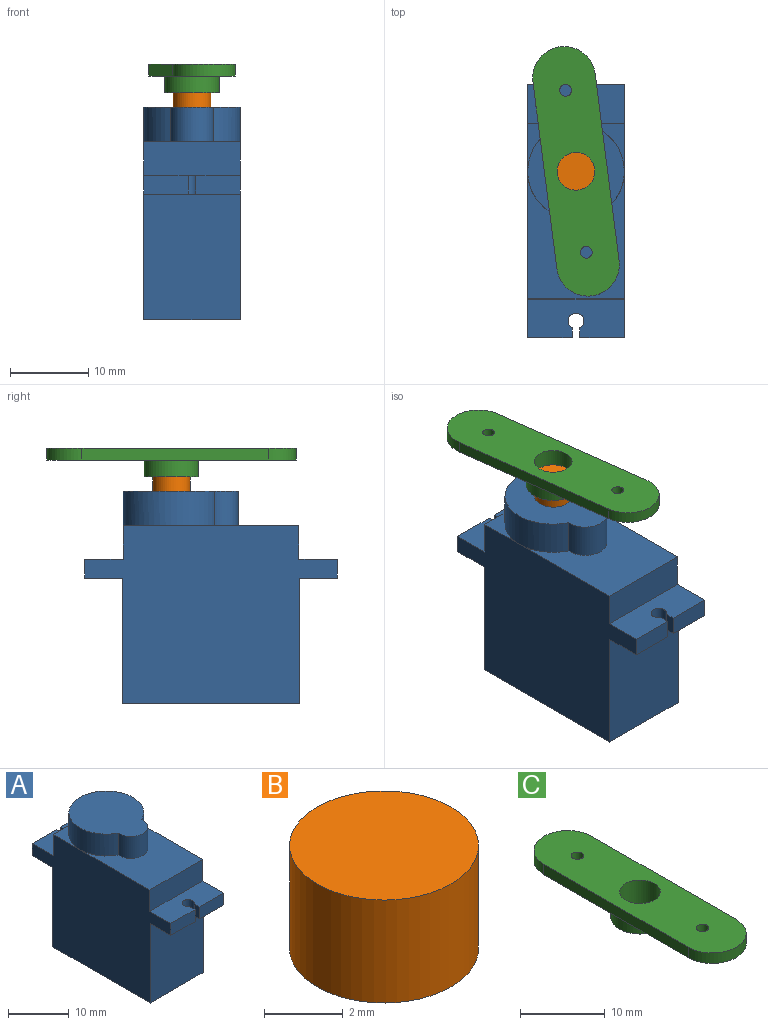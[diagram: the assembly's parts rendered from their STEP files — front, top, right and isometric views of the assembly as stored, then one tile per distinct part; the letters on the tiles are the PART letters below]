
ASSEMBLY  parts=3 mates=2
PART A: 27 faces, bbox 12.3x32.2x27.1 mm
  f0: plane 12.3x4.8mm, normal (0,0,-1), area 54.8mm2, adj f5,f11,f12,f13,f14,f15,f16,f24
  f1: plane 16.25x12.3mm, normal (0,0,1), area 129.6mm2, adj f5,f11,f19,f21,f22
  f2: plane 6.15x6.15mm, normal (0,0,1), area 8.1mm2, adj f5,f20,f21
  f3: plane 6.15x6.15mm, normal (0,0,1), area 8.1mm2, adj f11,f20,f21
  f4: plane 12.3x4.9mm, normal (0,0,1), area 56mm2, adj f5,f6,f7,f8,f9,f10,f11,f19
  f5: plane 32.2x22.7mm, normal (-1,0,0), area 535.2mm2, adj f0,f1,f2,f4,f6,f16,f17,f18
  f6: plane 5.65x2.4mm, normal (0,-1,0), area 13.6mm2, adj f4,f5,f7,f18
  f7: plane 2.4x1.23mm, normal (1,0,0), area 3mm2, adj f4,f6,f8,f18
  f8: cylinder r=1mm len=2.4mm, axis (0,0,-1), area 12.6mm2, adj f4,f7,f9,f18
  f9: plane 2.4x1.23mm, normal (-1,0,0), area 3mm2, adj f4,f8,f10,f18
  f10: plane 5.65x2.4mm, normal (0,-1,0), area 13.6mm2, adj f4,f9,f11,f18
  f11: plane 32.2x22.7mm, normal (1,0,0), area 535.2mm2, adj f0,f1,f3,f4,f10,f12,f17,f18
  f12: plane 5.65x2.4mm, normal (0,1,0), area 13.6mm2, adj f0,f11,f13,f17
  f13: plane 2.4x1.23mm, normal (-1,0,0), area 3mm2, adj f0,f12,f14,f17
  f14: cylinder r=1mm len=2.4mm, axis (0,0,-1), area 12.6mm2, adj f0,f13,f15,f17
  f15: plane 2.4x1.23mm, normal (1,0,0), area 3mm2, adj f0,f14,f16,f17
  f16: plane 5.65x2.4mm, normal (0,1,0), area 13.6mm2, adj f0,f5,f15,f17
  f17: plane 12.3x4.9mm, normal (0,0,1), area 56mm2, adj f5,f11,f12,f13,f14,f15,f16,f20
  f18: plane 12.3x4.8mm, normal (0,0,-1), area 54.8mm2, adj f5,f6,f7,f8,f9,f10,f11,f25
  f19: plane 12.3x4.3mm, normal (0,-1,0), area 52.9mm2, adj f1,f4,f5,f11
  f20: plane 12.3x4.3mm, normal (0,1,0), area 52.9mm2, adj f2,f3,f5,f11,f17
  f21: cylinder r=6.15mm len=12.3mm, axis (0,0,-1), area 145mm2, adj f1,f2,f3,f22,f23
  f22: cylinder r=2.75mm len=5.5mm, axis (0,0,-1), area 40.2mm2, adj f1,f21,f23
  f23: plane 14.65x12.3mm, normal (0,0,1), area 129.7mm2, adj f21,f22
  f24: plane 16x12.3mm, normal (0,1,0), area 196.8mm2, adj f0,f5,f11,f26
  f25: plane 16x12.3mm, normal (0,-1,0), area 196.8mm2, adj f5,f11,f18,f26
  f26: plane 22.6x12.3mm, normal (0,0,-1), area 278mm2, adj f5,f11,f24,f25
PART B: 3 faces, bbox 4.8x4.8x3.2 mm
  f0: cylinder r=2.4mm len=4.8mm, axis (0,0,-1), area 48.3mm2, adj f1,f2
  f1: plane 4.8x4.8mm, normal (0,0,1), area 18.1mm2, adj f0
  f2: plane 4.8x4.8mm, normal (0,0,-1), area 18.1mm2, adj f0
PART C: 11 faces, bbox 8x32x3.7 mm
  f0: plane 24x1.5mm, normal (1,0,0), area 36mm2, adj f5,f6,f9,f10
  f1: plane 24x1.5mm, normal (-1,0,0), area 36mm2, adj f5,f6,f9,f10
  f2: cylinder r=0.75mm len=1.5mm, axis (0,0,-1), area 7.1mm2, adj f5,f6
  f3: cylinder r=0.75mm len=1.5mm, axis (0,0,-1), area 7.1mm2, adj f5,f6
  f4: cylinder r=2.4mm len=4.8mm, axis (0,0,-1), area 55mm2, adj f5,f8
  f5: plane 32x8mm, normal (0,0,1), area 220.6mm2, adj f0,f1,f2,f3,f4,f9,f10
  f6: plane 32x8mm, normal (0,0,-1), area 201.3mm2, adj f0,f1,f2,f3,f7,f9,f10
  f7: cylinder r=3.45mm len=6.9mm, axis (0,0,1), area 46.6mm2, adj f6,f8
  f8: plane 6.9x6.9mm, normal (0,0,-1), area 19.3mm2, adj f4,f7
  f9: cylinder r=4mm len=8mm, axis (0,0,1), area 18.8mm2, adj f0,f1,f5,f6
  f10: cylinder r=4mm len=8mm, axis (0,0,-1), area 18.8mm2, adj f0,f1,f5,f6
PLACE A at identity fixed
PLACE B rot(axis=(0,0,-1),172.7deg) t=(-0.64,10.06,0)mm
PLACE C rot(axis=(0,0,-1),172.7deg) t=(-0.64,10.06,0.75)mm
MATE revolute A.f21 <-> B.f0  axis (0,0,1) through (0,5.05,11.1)mm
MATE slider C.f4 <-> B.f0  axis (0,0,1) through (0,5.05,14.3)mm
